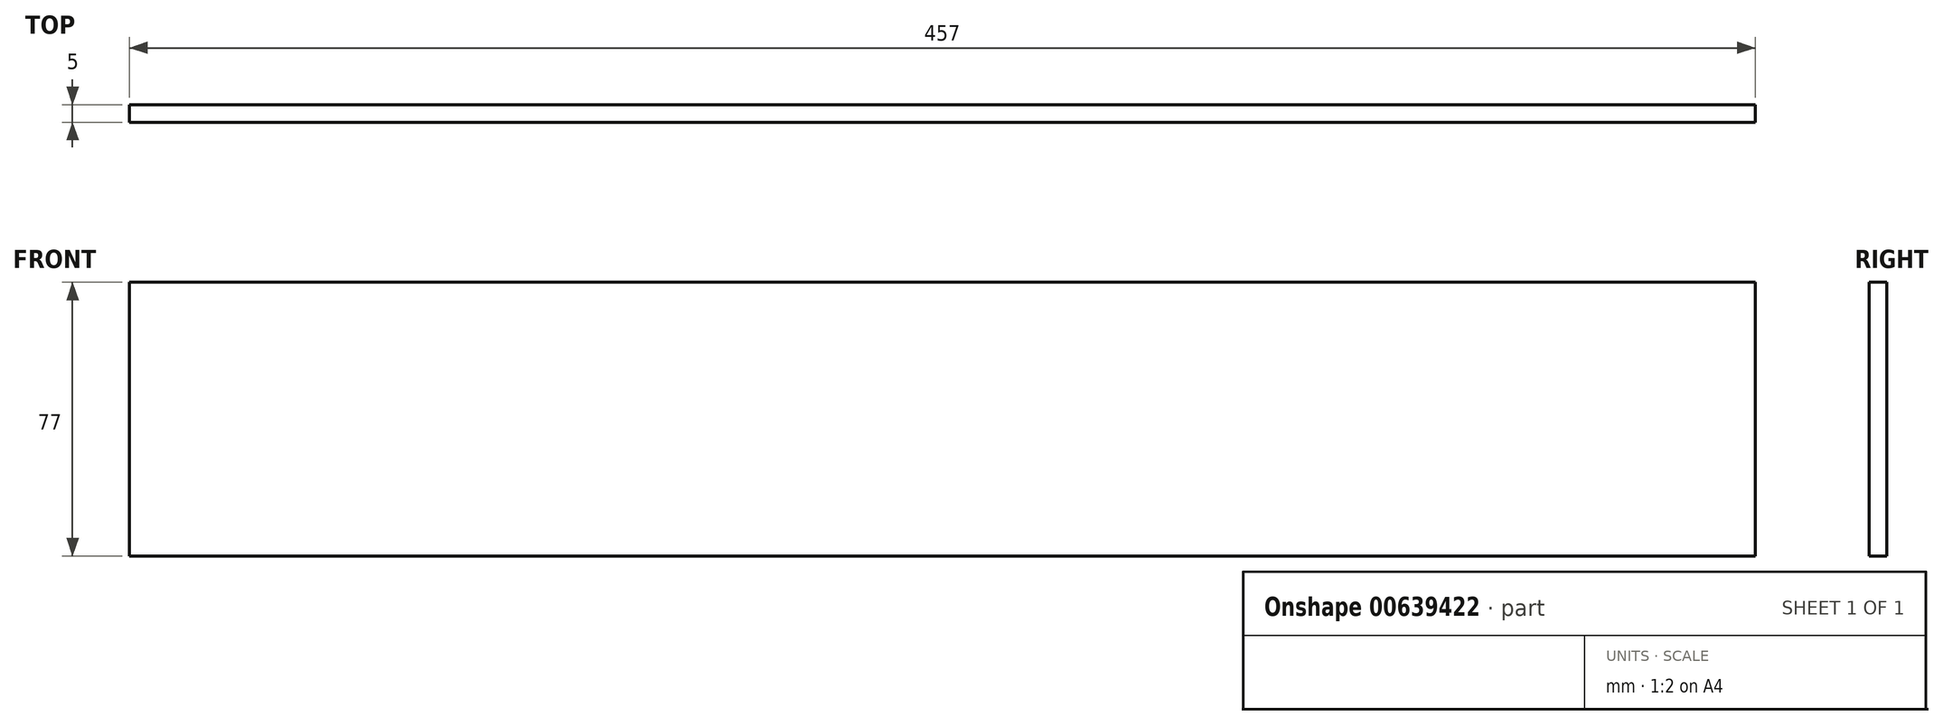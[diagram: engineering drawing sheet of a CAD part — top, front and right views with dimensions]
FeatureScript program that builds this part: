
annotation { "Feature Type Name" : "Feature", "Feature Type Description" : "" }
export const myFeature = defineFeature(function(context is Context, id is Id, definition is map)
    precondition{}
    {
        {
            var Q0;
            Q0=qCreatedBy(makeId("Front.planeOp"),FACE);
            var sketch = newSketch(context, id + "F0", { "sketchPlane" : qUnion([Q0])});
            skLineSegment(sketch, "E0.bottom", {"start": v(0, 0) * mm, "end": v(457, 0) * mm});
            skLineSegment(sketch, "E0.top", {"start": v(0, 77) * mm, "end": v(457, 77) * mm});
            skLineSegment(sketch, "E0.left", {"start": v(0, 0) * mm, "end": v(0, 77) * mm});
            skLineSegment(sketch, "E0.right", {"start": v(457, 0) * mm, "end": v(457, 77) * mm});
            skSolve(sketch);
        }
        {
            var Q0;
            Q0=makeQuery(id+"F0.imprint","IMPRINT",FACE,{"disambiguationData":[TD([[makeQuery(id+"F0.imprint","IMPRINT",EDGE,{"derivedFrom":sQuery(id+"F0.wireOp",EDGE,"E0.bottom")}),1.0]])]});
            extrude(context, id + "F1", {"entities" : qUnion([Q0]), "depth" : 5 * mm, "offsetDistance" : 25 * mm});
        }
    });
